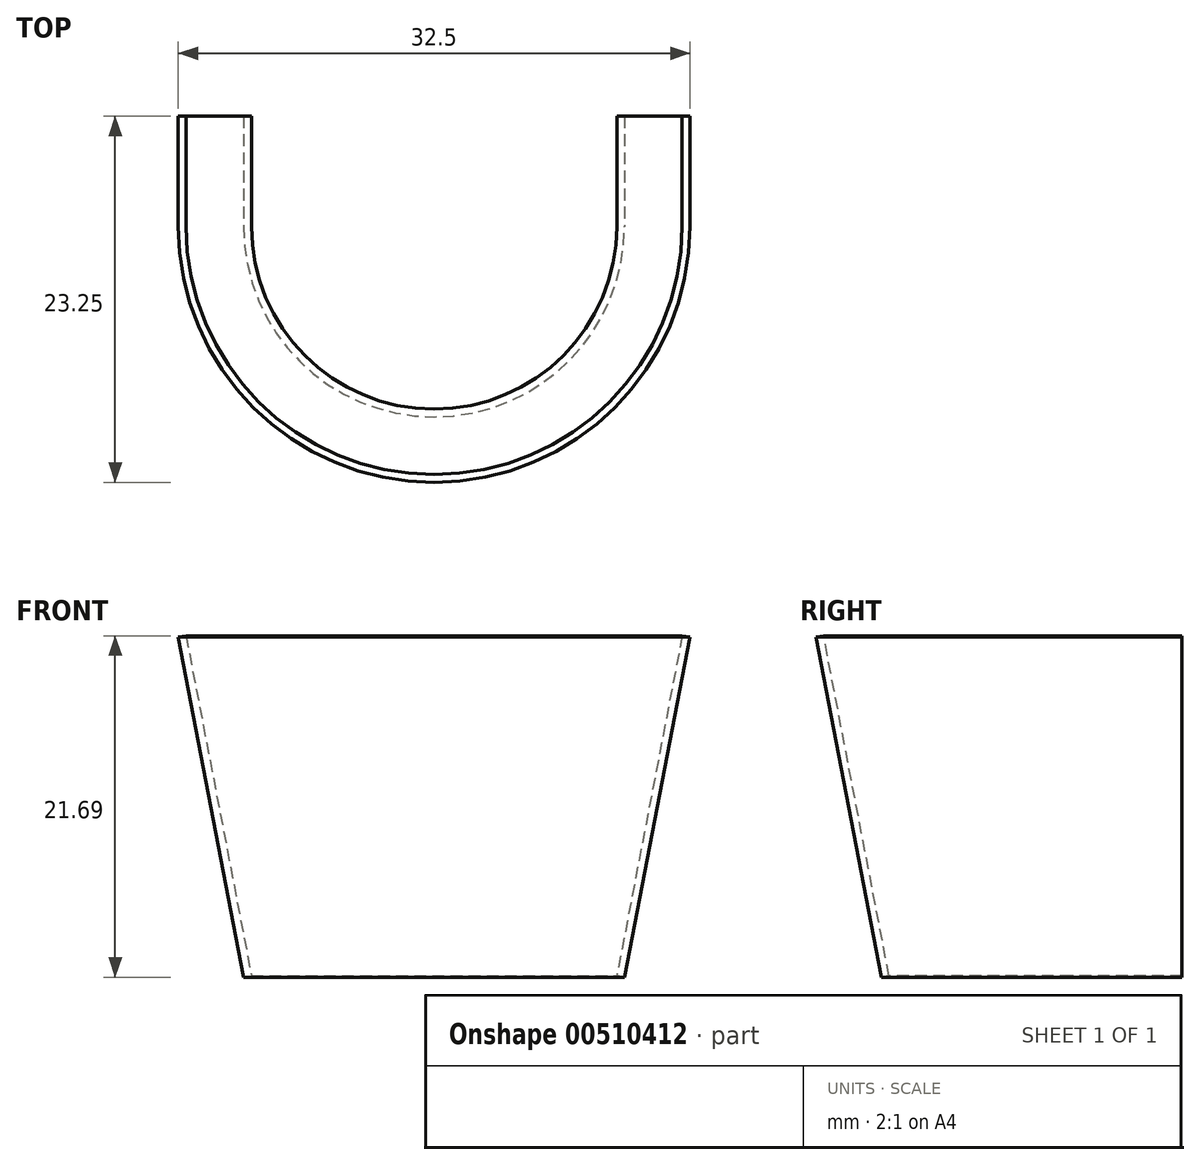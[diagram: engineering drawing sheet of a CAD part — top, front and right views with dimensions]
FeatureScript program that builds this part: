
annotation { "Feature Type Name" : "Feature", "Feature Type Description" : "" }
export const myFeature = defineFeature(function(context is Context, id is Id, definition is map)
    precondition{}
    {
        {
            var Q0;
            Q0=qCreatedBy(makeId("Right.planeOp"),FACE);
            var sketch = newSketch(context, id + "F0", { "sketchPlane" : qUnion([Q0])});
            skLineSegment(sketch, "E0", {"start": v(0, 0) * mm, "end": v(4.16, -21.6) * mm});
            skLineSegment(sketch, "E1", {"start": v(0, 0) * mm, "end": v(0.5, 0.1) * mm});
            skLineSegment(sketch, "E2", {"start": v(4.16, -21.6) * mm, "end": v(4.65, -21.5) * mm});
            skLineSegment(sketch, "E3", {"start": v(0.5, 0.1) * mm, "end": v(4.65, -21.5) * mm});
            skLineSegment(sketch, "E4.bottom", {"start": v(0, -22.48) * mm, "end": v(16.25, -22.48) * mm, "construction": true});
            skLineSegment(sketch, "E4.top", {"start": v(0, -39.43) * mm, "end": v(16.25, -39.43) * mm, "construction": true});
            skLineSegment(sketch, "E4.left", {"start": v(0, -22.48) * mm, "end": v(0, -39.43) * mm, "construction": true});
            skLineSegment(sketch, "E4.right", {"start": v(16.25, -22.48) * mm, "end": v(16.25, -39.43) * mm, "construction": true});
            skLineSegment(sketch, "E5", {"start": v(16.25, -22.48) * mm, "end": v(16.25, 8.38) * mm, "construction": true});
            skSolve(sketch);
        }
        {
            var Q0;
            Q0 = qSketchRegion(id + "F0", true);
            var Q1;
            Q1=sQuery(id+"F0.wireOp",EDGE,"E5");
            revolve(context, id + "F1", {"entities" : qUnion([Q0]), "axis" : qUnion([Q1]), "revolveType" : RevolveType.SYMMETRIC, "oppositeDirection" : true, "angle" : 180 * degree});
        }
        {
            var Q0;
            Q0=qCreatedBy(makeId("Front.planeOp"),FACE);
            var sketch = newSketch(context, id + "F2", { "sketchPlane" : qUnion([Q0])});
            skSolve(sketch);
        }
        {
            var Q0;
            Q0 = qSketchRegion(id + "F2", true);
            var Q1;
            Q1=makeQuery(id+"F1.opRevolve","CAP_FACE",FACE,{"disambiguationData":[OSD([sQuery(id+"F0.wireOp",EDGE,"E0"),sQuery(id+"F0.wireOp",EDGE,"E1"),sQuery(id+"F0.wireOp",EDGE,"E2"),sQuery(id+"F0.wireOp",EDGE,"E3")])],"isStart":true});
            var Q2;
            Q2=makeQuery(id+"F1.opRevolve","CAP_FACE",FACE,{"disambiguationData":[OSD([sQuery(id+"F0.wireOp",EDGE,"E0"),sQuery(id+"F0.wireOp",EDGE,"E1"),sQuery(id+"F0.wireOp",EDGE,"E2"),sQuery(id+"F0.wireOp",EDGE,"E3")])],"isStart":false});
            extrude(context, id + "F3", {"entities" : qUnion([Q0, Q1, Q2]), "operationType" : NewBodyOperationType.ADD, "depth" : 7 * mm});
        }
    });
